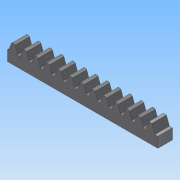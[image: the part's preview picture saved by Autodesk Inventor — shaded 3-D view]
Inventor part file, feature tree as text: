
AUTODESK INVENTOR PART (.ipt)
format: ipt  version: 2015 (Build 190159000, 159)  size: 1,329,664 bytes
history: native  units: in
note: dims shown in document units (in); Inventor stores cm internally (conversion verified against a paired STEP export)
features: plane x3, extrude x3, sketch x3, projected_geometry x2, other x1, fillet x1
ambient origin geometry x8: Origin, YZ Plane, XZ Plane, XY Plane, X Axis, Y Axis, Z Axis, Center Point
bodies: Volumenkörper1 (feature_tree)
feature tree (13):
  other  "101000_ss"
  plane  "Arbeitsebene1"
  extrude  "Extrusion1"  Depth=0.0394in
  plane  "Arbeitsebene2"
  extrude  "Extrusion2"  Depth=0.0394in
  plane  "Arbeitsebene3"
  extrude  "Extrusion3"  Depth=0.3937in TaperAngle=0.0deg
  fillet  "Rundung1"  Radius=0.3937in
  sketch  "Skizze1"  dims[d0=-1.626in d1=0.0394in]
  sketch  "Skizze2"  dims[d2=0.0394in d3=0.0394in]
  projected_geometry  "Projizierte Kontur1"
  sketch  "Skizze3"  dims[d4=0.0394in d5=0.3937in d6=0.0in d7=0.3937in d8=0.0in d9=0.3937in d10=0.0in d11=0.0157in d12=0.0118in]
  projected_geometry  "Projizierte Kontur2"
